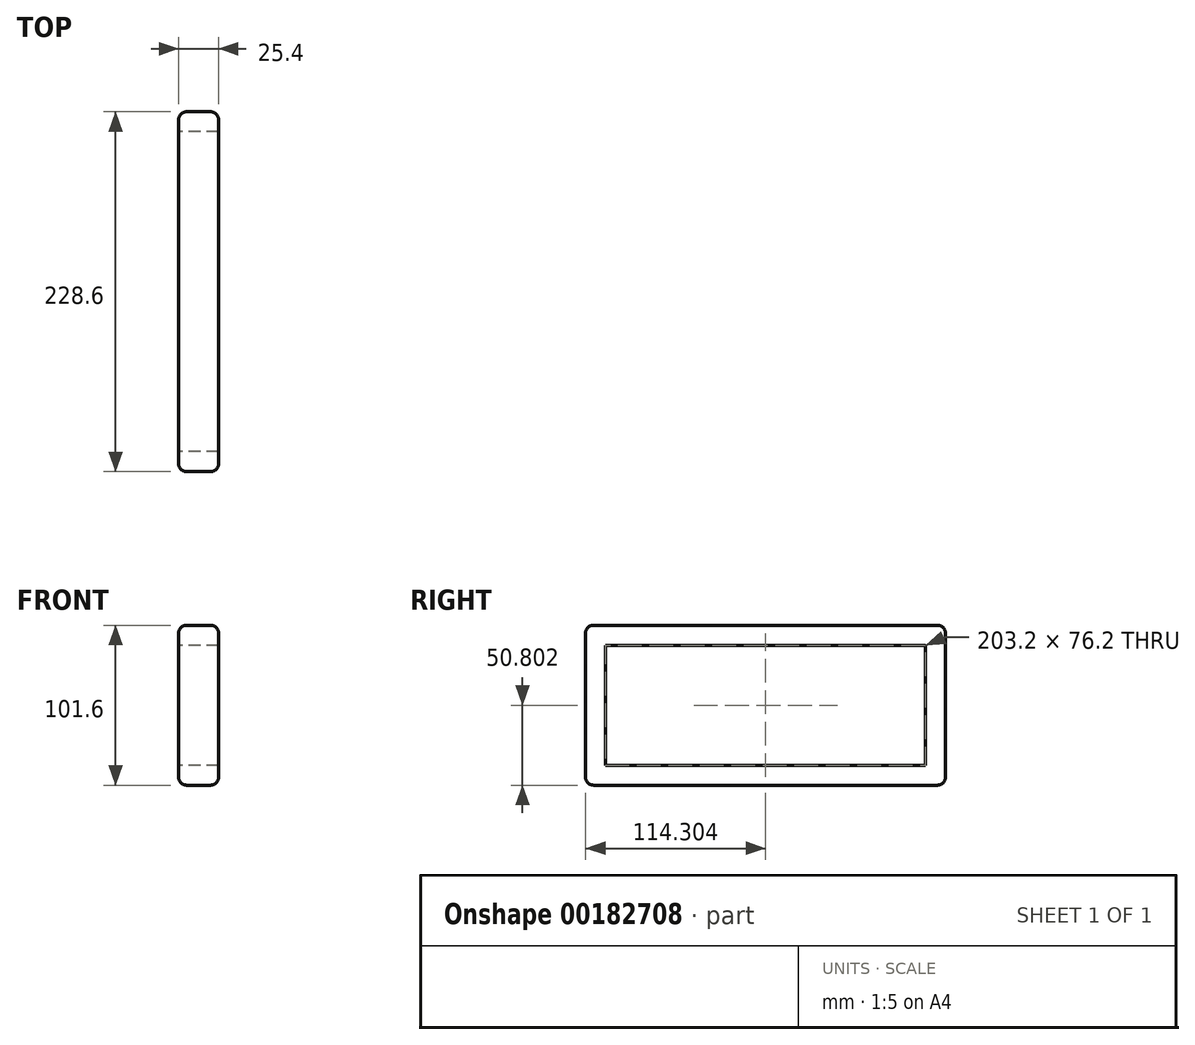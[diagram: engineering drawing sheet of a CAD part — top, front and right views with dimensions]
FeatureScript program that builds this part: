
annotation { "Feature Type Name" : "Feature", "Feature Type Description" : "" }
export const myFeature = defineFeature(function(context is Context, id is Id, definition is map)
    precondition{}
    {
        {
            var Q0;
            Q0=qCreatedBy(makeId("Right.planeOp"),FACE);
            var sketch = newSketch(context, id + "F0", { "sketchPlane" : qUnion([Q0])});
            skLineSegment(sketch, "E0.bottom", {"start": v(-109.64, 54.36) * mm, "end": v(118.96, 54.36) * mm});
            skLineSegment(sketch, "E0.top", {"start": v(-109.64, -47.24) * mm, "end": v(118.96, -47.24) * mm});
            skLineSegment(sketch, "E0.left", {"start": v(-109.64, 54.36) * mm, "end": v(-109.64, -47.24) * mm});
            skLineSegment(sketch, "E0.right", {"start": v(118.96, 54.36) * mm, "end": v(118.96, -47.24) * mm});
            skLineSegment(sketch, "E1.bottom", {"start": v(-96.94, 41.66) * mm, "end": v(106.26, 41.66) * mm});
            skLineSegment(sketch, "E1.top", {"start": v(-96.94, -34.54) * mm, "end": v(106.26, -34.54) * mm});
            skLineSegment(sketch, "E1.left", {"start": v(-96.94, 41.66) * mm, "end": v(-96.94, -34.54) * mm});
            skLineSegment(sketch, "E1.right", {"start": v(106.26, 41.66) * mm, "end": v(106.26, -34.54) * mm});
            skSolve(sketch);
        }
        {
            var Q0;
            Q0=makeQuery(id+"F0.imprint","IMPRINT",FACE,{"disambiguationData":[TD([[makeQuery(id+"F0.imprint","IMPRINT",EDGE,{"derivedFrom":sQuery(id+"F0.wireOp",EDGE,"E0.bottom")}),-1.0]])]});
            extrude(context, id + "F1", {"entities" : qUnion([Q0]), "depth" : 25.4 * mm});
        }
        {
            var Q0;
            Q0=makeQuery(id+"F1.opExtrude","SWEPT_FACE",FACE,{"disambiguationData":[OSD([sQuery(id+"F0.wireOp",EDGE,"E0.bottom")])]});
            var Q1;
            Q1=makeQuery(id+"F1.opExtrude","SWEPT_FACE",FACE,{"disambiguationData":[OSD([sQuery(id+"F0.wireOp",EDGE,"E0.left")])]});
            var Q2;
            Q2=makeQuery(id+"F1.opExtrude","SWEPT_FACE",FACE,{"disambiguationData":[OSD([sQuery(id+"F0.wireOp",EDGE,"E0.right")])]});
            var Q3;
            Q3=makeQuery(id+"F1.opExtrude","SWEPT_FACE",FACE,{"disambiguationData":[OSD([sQuery(id+"F0.wireOp",EDGE,"E0.top")])]});
            fillet(context, id + "F2", {"entities" : qUnion([Q0, Q1, Q2, Q3]), "radius" : 5.08 * mm, "tangentPropagation" : true, "allowEdgeOverflow" : false});
        }
    });
